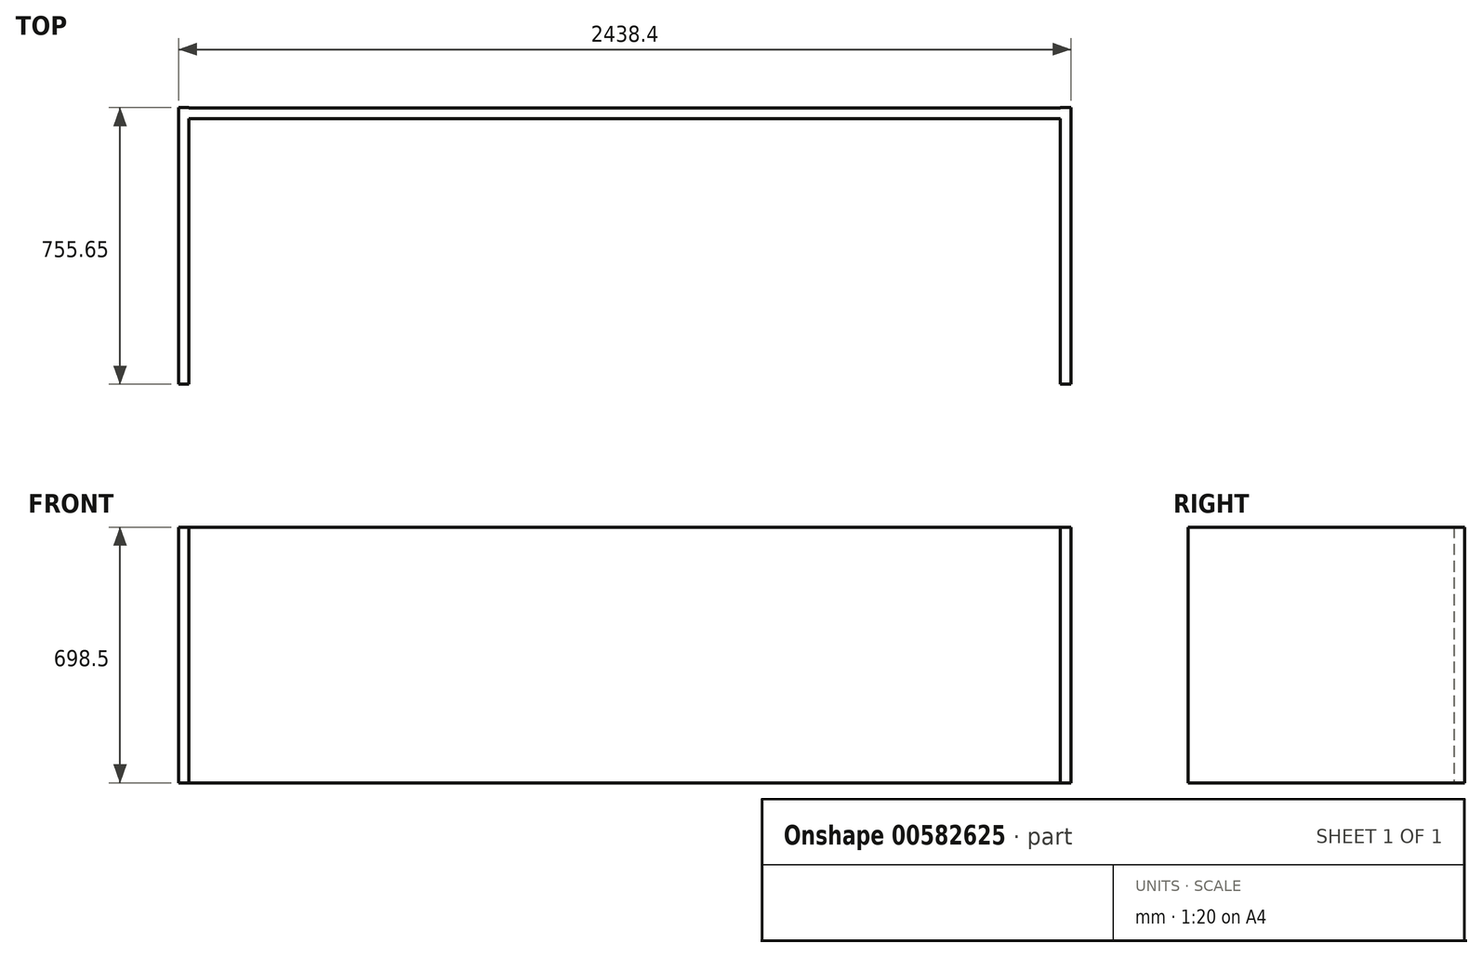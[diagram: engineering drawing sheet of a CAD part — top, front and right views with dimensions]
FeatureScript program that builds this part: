
annotation { "Feature Type Name" : "Feature", "Feature Type Description" : "" }
export const myFeature = defineFeature(function(context is Context, id is Id, definition is map)
    precondition{}
    {
        {
            var Q0;
            Q0=qCreatedBy(makeId("Top.planeOp"),FACE);
            var sketch = newSketch(context, id + "F0", { "sketchPlane" : qUnion([Q0])});
            skLineSegment(sketch, "E0.bottom", {"start": v(2124.46, 56.07) * mm, "end": v(-256.79, 56.07) * mm});
            skLineSegment(sketch, "E0.top", {"start": v(2124.46, 84.65) * mm, "end": v(-256.79, 84.65) * mm});
            skLineSegment(sketch, "E0.left", {"start": v(2124.46, 56.07) * mm, "end": v(2124.46, 84.65) * mm});
            skLineSegment(sketch, "E0.right", {"start": v(-256.79, 56.07) * mm, "end": v(-256.79, 84.65) * mm});
            skPoint(sketch, "E0.middle", {"position": v(933.84, 70.36) * mm});
            skSolve(sketch);
        }
        {
            var Q0;
            Q0 = qSketchRegion(id + "F0", true);
            extrude(context, id + "F1", {"entities" : qUnion([Q0]), "depth" : 698.5 * mm, "offsetDistance" : 25.4 * mm});
        }
        {
            var Q0;
            Q0=makeQuery(id+"F1.opExtrude","SWEPT_FACE",FACE,{"disambiguationData":[OSD([sQuery(id+"F0.wireOp",EDGE,"E0.left")])]});
            var sketch = newSketch(context, id + "F2", { "sketchPlane" : qUnion([Q0])});
            skLineSegment(sketch, "E1", {"start": v(84.65, 698.5) * mm, "end": v(85.41, 698.5) * mm});
            skLineSegment(sketch, "E2.bottom", {"start": v(85.41, 698.5) * mm, "end": v(-670.24, 698.5) * mm});
            skLineSegment(sketch, "E2.top", {"start": v(85.41, 0) * mm, "end": v(-670.24, 0) * mm});
            skLineSegment(sketch, "E2.left", {"start": v(85.41, 698.5) * mm, "end": v(85.41, 0) * mm});
            skLineSegment(sketch, "E2.right", {"start": v(-670.24, 698.5) * mm, "end": v(-670.24, 0) * mm});
            skSolve(sketch);
        }
        {
            var Q0;
            Q0=makeQuery(id+"F1.opExtrude","SWEPT_FACE",FACE,{"disambiguationData":[OSD([sQuery(id+"F0.wireOp",EDGE,"E0.right")])]});
            var sketch = newSketch(context, id + "F3", { "sketchPlane" : qUnion([Q0])});
            skLineSegment(sketch, "E3", {"start": v(-84.65, 698.5) * mm, "end": v(-85.41, 698.5) * mm});
            skLineSegment(sketch, "E4.bottom", {"start": v(-85.41, 698.5) * mm, "end": v(670.24, 698.5) * mm});
            skLineSegment(sketch, "E4.top", {"start": v(-85.41, 0) * mm, "end": v(670.24, 0) * mm});
            skLineSegment(sketch, "E4.left", {"start": v(-85.41, 698.5) * mm, "end": v(-85.41, 0) * mm});
            skLineSegment(sketch, "E4.right", {"start": v(670.24, 698.5) * mm, "end": v(670.24, 0) * mm});
            skSolve(sketch);
        }
        {
            var Q0;
            {var subQ2=sQuery(id+"F3.wireOp",EDGE,"E4.right");Q0=makeQuery(id+"F3.imprint","IMPRINT",FACE,{"disambiguationData":[TD([[makeQuery(id+"F3.imprint","IMPRINT",EDGE,{"derivedFrom":subQ2}),-1.0]])]});}
            var Q1;
            {var subQ1=sQuery(id+"F0.wireOp",EDGE,"E0.right");var subQ2=makeQuery(id+"F1.opExtrude","SWEPT_EDGE",EDGE,{"disambiguationData":[OSD([sQuery(id+"F0.wireOp",EDGE,"E0.bottom"),subQ1])]});Q1=makeQuery(id+"F3.imprint","IMPRINT",FACE,{"disambiguationData":[TD([[makeQuery(id+"F3.imprint","IMPRINT",EDGE,{"derivedFrom":subQ2}),-1.0]])]});}
            var Q2;
            {var subQ2=sQuery(id+"F3.wireOp",EDGE,"E4.left");Q2=makeQuery(id+"F3.imprint","IMPRINT",FACE,{"disambiguationData":[TD([[makeQuery(id+"F3.imprint","IMPRINT",EDGE,{"derivedFrom":subQ2}),1.0]])]});}
            extrude(context, id + "F4", {"entities" : qUnion([Q0, Q1, Q2]), "operationType" : NewBodyOperationType.ADD, "depth" : 28.57 * mm, "offsetDistance" : 25.4 * mm});
        }
        {
            var Q0;
            {var subQ2=sQuery(id+"F2.wireOp",EDGE,"E2.right");Q0=makeQuery(id+"F2.imprint","IMPRINT",FACE,{"disambiguationData":[TD([[makeQuery(id+"F2.imprint","IMPRINT",EDGE,{"derivedFrom":subQ2}),1.0]])]});}
            var Q1;
            {var subQ1=sQuery(id+"F0.wireOp",EDGE,"E0.left");var subQ2=makeQuery(id+"F1.opExtrude","SWEPT_EDGE",EDGE,{"disambiguationData":[OSD([sQuery(id+"F0.wireOp",EDGE,"E0.bottom"),subQ1])]});Q1=makeQuery(id+"F2.imprint","IMPRINT",FACE,{"disambiguationData":[TD([[makeQuery(id+"F2.imprint","IMPRINT",EDGE,{"derivedFrom":subQ2}),1.0]])]});}
            var Q2;
            {var subQ2=sQuery(id+"F2.wireOp",EDGE,"E2.left");Q2=makeQuery(id+"F2.imprint","IMPRINT",FACE,{"disambiguationData":[TD([[makeQuery(id+"F2.imprint","IMPRINT",EDGE,{"derivedFrom":subQ2}),-1.0]])]});}
            extrude(context, id + "F5", {"entities" : qUnion([Q0, Q1, Q2]), "operationType" : NewBodyOperationType.ADD, "depth" : 28.57 * mm, "offsetDistance" : 25.4 * mm});
        }
    });
